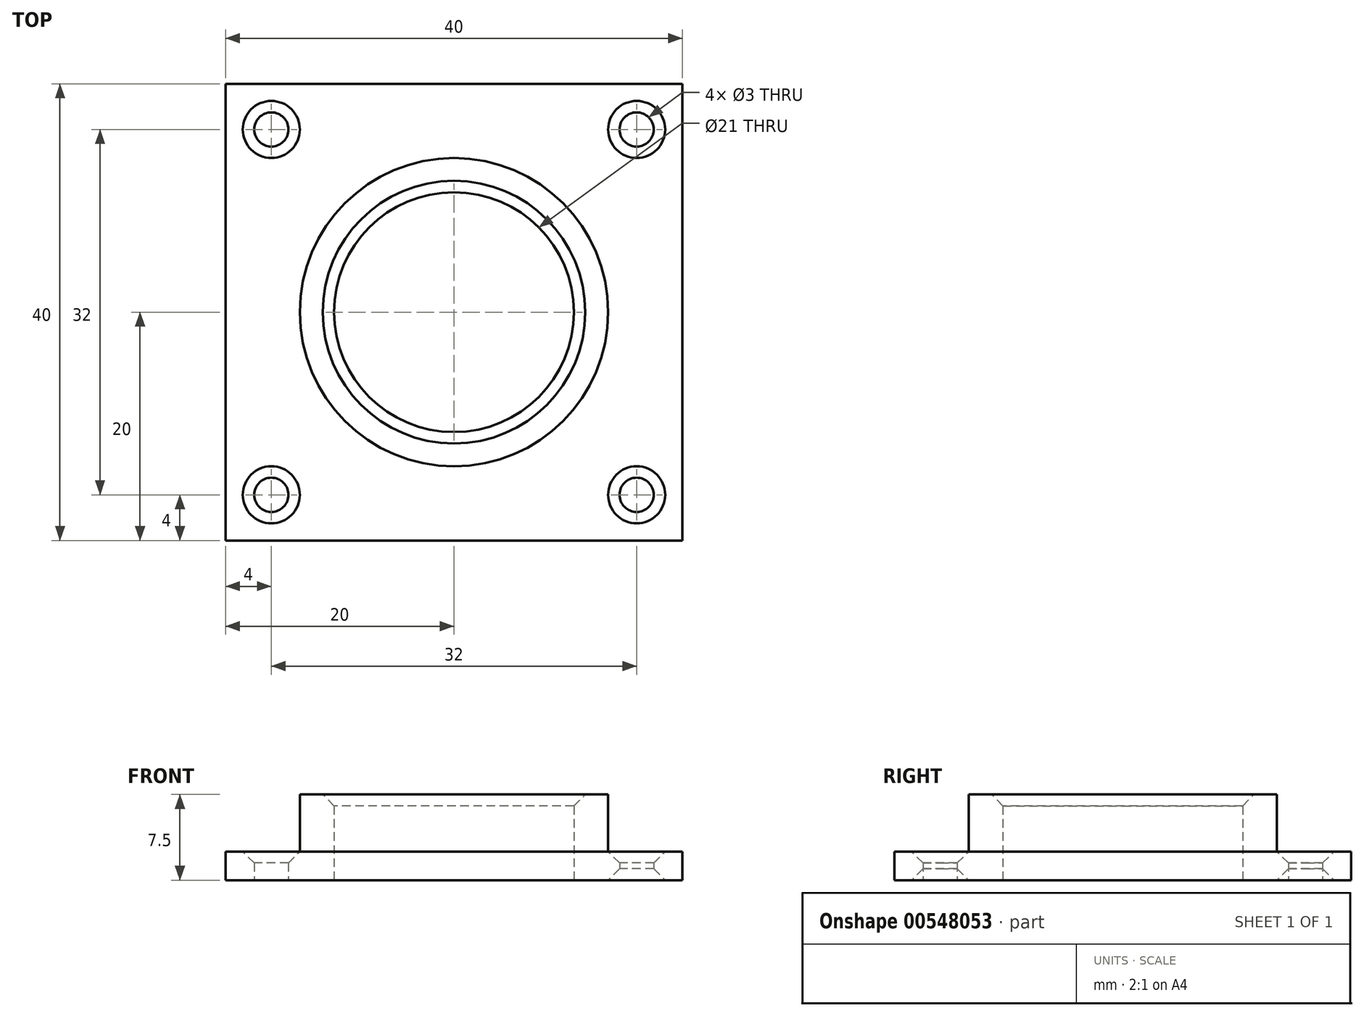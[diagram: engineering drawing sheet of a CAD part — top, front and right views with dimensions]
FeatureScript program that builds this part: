
annotation { "Feature Type Name" : "Feature", "Feature Type Description" : "" }
export const myFeature = defineFeature(function(context is Context, id is Id, definition is map)
    precondition{}
    {
        {
            var Q0;
            Q0=qCreatedBy(makeId("Top.planeOp"),FACE);
            var sketch = newSketch(context, id + "F0", { "sketchPlane" : qUnion([Q0])});
            skLineSegment(sketch, "E0.bottom", {"start": v(20, 20) * mm, "end": v(-20, 20) * mm});
            skLineSegment(sketch, "E0.top", {"start": v(20, -20) * mm, "end": v(-20, -20) * mm});
            skLineSegment(sketch, "E0.left", {"start": v(20, 20) * mm, "end": v(20, -20) * mm});
            skLineSegment(sketch, "E0.right", {"start": v(-20, 20) * mm, "end": v(-20, -20) * mm});
            skPoint(sketch, "E0.middle", {"position": v(0, 0) * mm});
            skCircle(sketch, "E1", {"center": v(-16, 16) * mm, "radius": 1.5 * mm});
            skCircle(sketch, "E2", {"center": v(16, 16) * mm, "radius": 1.5 * mm});
            skCircle(sketch, "E3", {"center": v(16, -16) * mm, "radius": 1.5 * mm});
            skCircle(sketch, "E4", {"center": v(-16, -16) * mm, "radius": 1.5 * mm});
            skCircle(sketch, "E5", {"center": v(0, 0) * mm, "radius": 10.5 * mm});
            skCircle(sketch, "E6.0", {"center": v(0, 0) * mm, "radius": 13.5 * mm});
            skSolve(sketch);
        }
        {
            var Q0;
            Q0 = qSketchRegion(id + "F0", true);
            extrude(context, id + "F1", {"entities" : qUnion([Q0]), "depth" : 2.5 * mm, "offsetDistance" : 25 * mm});
        }
        {
            var Q0;
            Q0=makeQuery(id+"F0.imprint","IMPRINT",FACE,{"disambiguationData":[TD([[makeQuery(id+"F0.imprint","IMPRINT",EDGE,{"derivedFrom":sQuery(id+"F0.wireOp",EDGE,"E5")}),-1.0]])]});
            extrude(context, id + "F2", {"entities" : qUnion([Q0]), "operationType" : NewBodyOperationType.ADD, "depth" : 7.5 * mm, "offsetDistance" : 25 * mm});
        }
        {
            var Q0;
            Q0=makeQuery(id+"F2.opExtrude","CAP_EDGE",EDGE,{"disambiguationData":[OSD([sQuery(id+"F0.wireOp",EDGE,"E5")])],"isStart":false});
            chamfer(context, id + "F3", {"entities" : qUnion([Q0]), "width" : 1 * mm, "tangentPropagation" : true});
        }
        {
            var Q0;
            Q0=makeQuery(id+"F1.opExtrude","CAP_EDGE",EDGE,{"disambiguationData":[OSD([sQuery(id+"F0.wireOp",EDGE,"E4")])],"isStart":false});
            chamfer(context, id + "F4", {"entities" : qUnion([Q0]), "width" : 1 * mm, "tangentPropagation" : true});
        }
        {
            var Q0;
            Q0=makeQuery(id+"F1.opExtrude","SWEPT_FACE",FACE,{"disambiguationData":[OSD([sQuery(id+"F0.wireOp",EDGE,"E3")])]});
            var Q1;
            Q1=makeQuery(id+"F1.opExtrude","SWEPT_FACE",FACE,{"disambiguationData":[OSD([sQuery(id+"F0.wireOp",EDGE,"E2")])]});
            var Q2;
            Q2=makeQuery(id+"F1.opExtrude","CAP_EDGE",EDGE,{"disambiguationData":[OSD([sQuery(id+"F0.wireOp",EDGE,"E1")])],"isStart":false});
            chamfer(context, id + "F5", {"entities" : qUnion([Q0, Q1, Q2]), "width" : 1 * mm, "tangentPropagation" : true});
        }
    });
